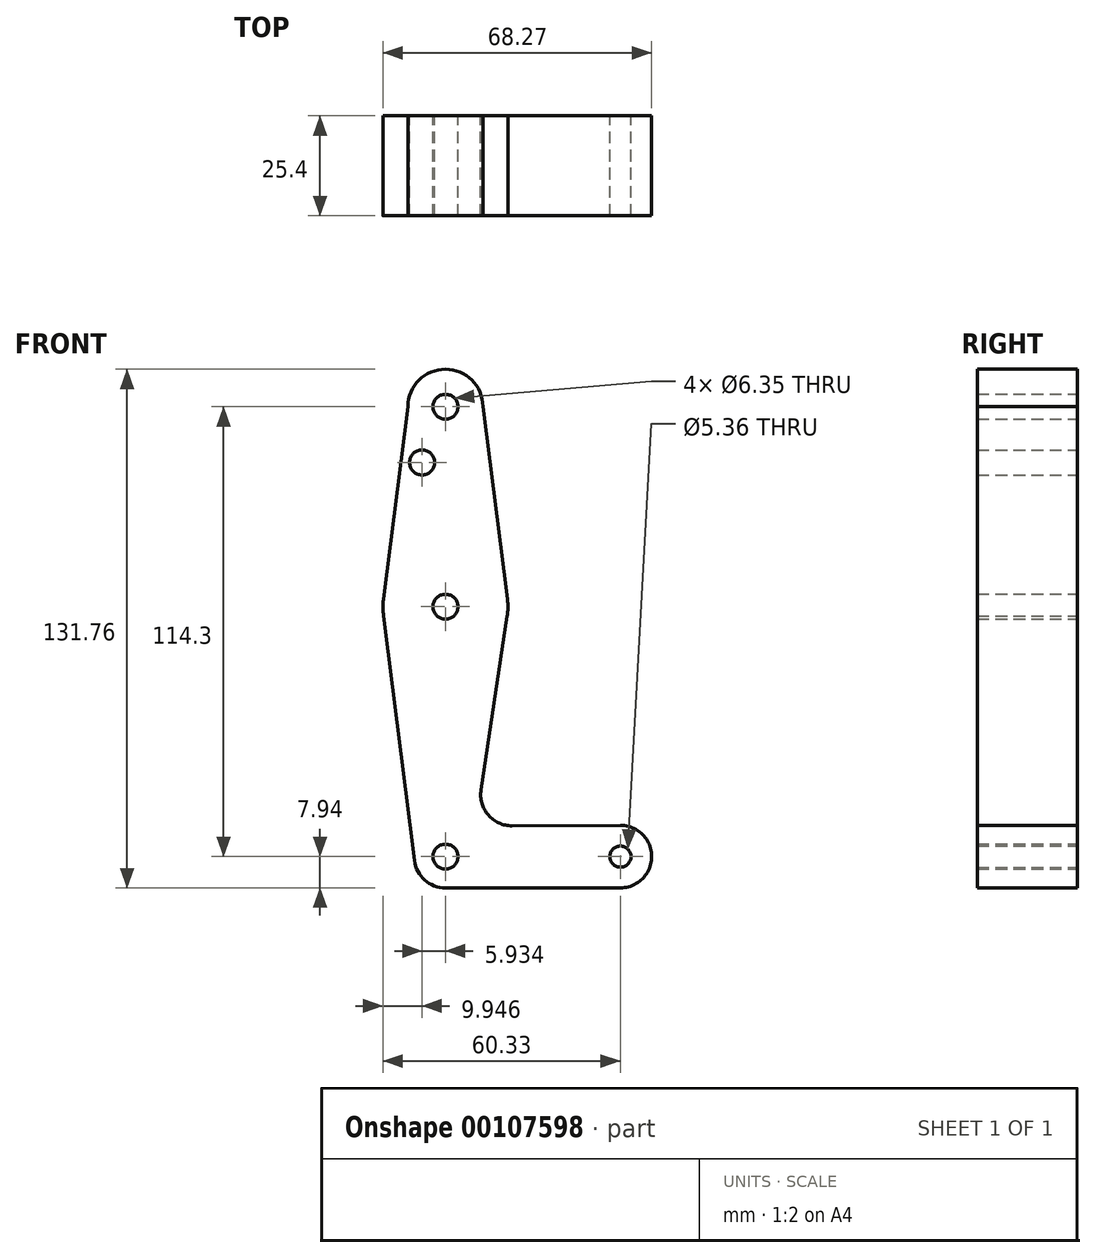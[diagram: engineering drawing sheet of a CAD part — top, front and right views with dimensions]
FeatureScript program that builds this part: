
annotation { "Feature Type Name" : "Feature", "Feature Type Description" : "" }
export const myFeature = defineFeature(function(context is Context, id is Id, definition is map)
    precondition{}
    {
        {
            var Q0;
            Q0=qCreatedBy(makeId("Front.planeOp"),FACE);
            var sketch = newSketch(context, id + "F0", { "sketchPlane" : qUnion([Q0])});
            skLineSegment(sketch, "E0", {"start": v(0, 50.8) * mm, "end": v(0, -63.5) * mm});
            skLineSegment(sketch, "E1", {"start": v(0, -55.75) * mm, "end": v(0, -63.5) * mm});
            skCircle(sketch, "E2", {"center": v(0, 50.8) * mm, "radius": 9.53 * mm});
            skCircle(sketch, "E3", {"center": v(0, 0) * mm, "radius": 15.88 * mm});
            skLineSegment(sketch, "E4", {"start": v(0, 0) * mm, "end": v(0, -63.5) * mm});
            skCircle(sketch, "E5", {"center": v(44.45, -63.5) * mm, "radius": 7.94 * mm});
            skCircle(sketch, "E6", {"center": v(0, -63.5) * mm, "radius": 3.18 * mm});
            skCircle(sketch, "E7", {"center": v(44.45, -63.5) * mm, "radius": 2.68 * mm});
            skCircle(sketch, "E8", {"center": v(0, 0) * mm, "radius": 3.18 * mm});
            skCircle(sketch, "E9", {"center": v(0, 50.8) * mm, "radius": 3.18 * mm});
            skCircle(sketch, "E10", {"center": v(0, -63.5) * mm, "radius": 7.94 * mm});
            skLineSegment(sketch, "E11", {"start": v(-9.52, 50.88) * mm, "end": v(-15.75, 2) * mm});
            skLineSegment(sketch, "E12", {"start": v(-15.7, -2.32) * mm, "end": v(-7.88, -64.5) * mm});
            skLineSegment(sketch, "E13", {"start": v(9.52, 50.87) * mm, "end": v(15.75, 2) * mm});
            skLineSegment(sketch, "E14", {"start": v(0, -71.44) * mm, "end": v(44.45, -71.44) * mm});
            skLineSegment(sketch, "E15", {"start": v(0, 0) * mm, "end": v(0, 36.53) * mm});
            skLineSegment(sketch, "E16", {"start": v(16.94, -55.68) * mm, "end": v(44.42, -55.56) * mm});
            skLineSegment(sketch, "E17", {"start": v(15.7, -2.37) * mm, "end": v(9.04, -46.54) * mm});
            skArc(sketch, "E18.filletArc", {"start": v(9.04, -46.54) * mm, "mid": v(10.89, -52.93) * mm, "end": v(16.94, -55.68) * mm});
            skCircle(sketch, "E19", {"center": v(-5.93, 36.65) * mm, "radius": 3.18 * mm});
            skSolve(sketch);
        }
        {
            var Q0;
            Q0 = qSketchRegion(id + "F0", true);
            extrude(context, id + "F1", {"entities" : qUnion([Q0]), "depth" : 25.4 * mm});
        }
        {
            var Q0;
            Q0 = qSketchRegion(id + "F0", true);
            extrude(context, id + "F2", {"entities" : qUnion([Q0]), "operationType" : NewBodyOperationType.ADD, "depth" : 25.4 * mm});
        }
        {
            var Q0;
            Q0 = qSketchRegion(id + "F0", true);
            extrude(context, id + "F3", {"entities" : qUnion([Q0]), "operationType" : NewBodyOperationType.ADD, "depth" : 25.4 * mm});
        }
    });
